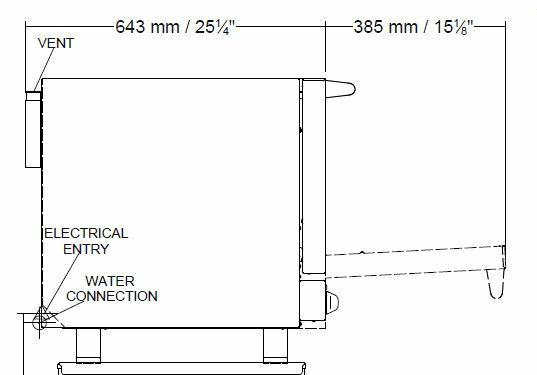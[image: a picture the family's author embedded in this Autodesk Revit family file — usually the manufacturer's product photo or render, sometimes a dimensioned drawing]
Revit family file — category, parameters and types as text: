
# Revit family: QF_MOFFAT_E23D3-2C_NZ
name_source: partatom
category: Specialty Equipment
revit_build: Autodesk Revit 2014 (Build: 20130308_1515(x64)
units: mm (PartAtom-declared; Revit-internal decimal feet)

## types (1)
- QF_MOFFAT_E23D3-2C_NZ
    Apparent Power = 2760 VA
    Cold Water Connection Height = 0 mm  [stored 0 ft]
    Cold Water Flow = 0 GPM
    Cold Water Maximum Pressure = 80.00 psi
    Cold Water Minimum Pressure = 20.00 psi
    Cold Water RI Height = 0 mm  [stored 0 ft]
    Cold Water Size = 1"
    Cold Water Temperature Recommended = 0 °F
    Conn Conduit = Yes
    Cycle = 50 Hz
    Depth = 643 mm  [stored 2.10958 ft]
    Description = HALF SIZE DIGITAL / ELECTRIC CONVECTION OVENS DOUBLE STACKED ON A STAINLESS STEEL BASE STAND
    Elec Conn Connection Height = 0 mm  [stored 0 ft]
    Elec Conn RI Height = 0 mm  [stored 0 ft]
    Electrical Remarks = 230-240V, 50Hz, 1P+N+E, 3.0kW, 12A
    Exhaust RI Height = 0 mm  [stored 0 ft]
    Exhaust Static Press = 0.00 in-wg
    Exhaust Vent Depth = 0 mm  [stored 0 ft]
    Exhaust Vent Diameter = 0 mm  [stored 0 ft]
    Exhaust Vent Width = 0 mm  [stored 0 ft]
    Exhaust Volume = 0 CFM
    FL Amps = 12 A
    Foodservice Equipment Identifier = Yes
    Height = 1653 mm  [stored 5.42323 ft]
    Height of Stand = 536 mm  [stored 1.75853 ft]
    Identify Quantity as Lot = Yes
    Length = 610 mm  [stored 2.00131 ft]
    Manufacturer = MOFFAT
    Max Overcurrent Protection = 0 A
    Min Ckt Ampacity = 0 A
    Model = E23D3-2C
    Number of Poles = 1
    Phase = 1
    URL = www.moffat.com.au
    URL Cutsheet = www.moffat.com.au
    Volts = 230 V
    Watts = 3000 W
    Weight in Pounds = 0

note: [stored X ft] marks values corroborated as IEEE doubles in the binary element streams (Revit-internal decimal feet)

## geometry (parser evidence)
native form markers: Blend x16, Sweep x12
no freeform markers — native parametric forms only
